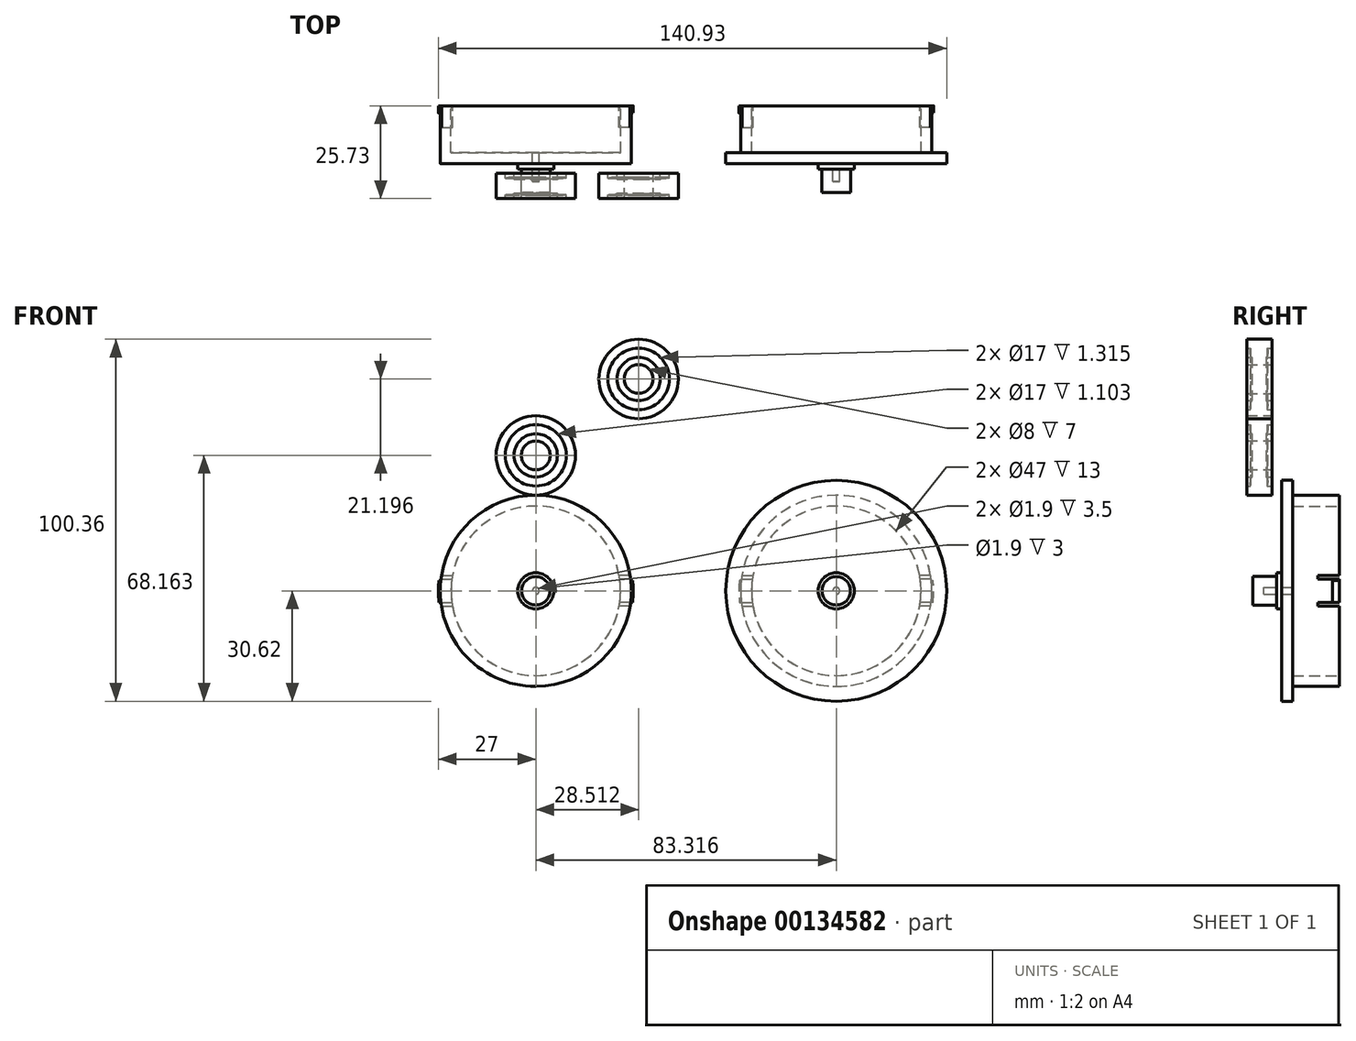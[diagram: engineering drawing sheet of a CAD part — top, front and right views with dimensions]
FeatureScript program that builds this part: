
annotation { "Feature Type Name" : "Feature", "Feature Type Description" : "" }
export const myFeature = defineFeature(function(context is Context, id is Id, definition is map)
    precondition{}
    {
        {
            var Q0;
            Q0=qCreatedBy(makeId("Front.planeOp"),FACE);
            var sketch = newSketch(context, id + "F0", { "sketchPlane" : qUnion([Q0])});
            skCircle(sketch, "E0", {"center": v(0, 0) * mm, "radius": 26.5 * mm});
            skSolve(sketch);
        }
        {
            var Q0;
            Q0 = qSketchRegion(id + "F0", true);
            extrude(context, id + "F1", {"entities" : qUnion([Q0]), "depth" : 16 * mm});
        }
        {
            var Q0;
            Q0=qCreatedBy(makeId("Front.planeOp"),FACE);
            var sketch = newSketch(context, id + "F2", { "sketchPlane" : qUnion([Q0])});
            skCircle(sketch, "E1", {"center": v(0, 0) * mm, "radius": 3.95 * mm});
            skSolve(sketch);
        }
        {
            var Q0;
            Q0 = qSketchRegion(id + "F2", true);
            extrude(context, id + "F3", {"entities" : qUnion([Q0]), "operationType" : NewBodyOperationType.ADD, "depth" : 24 * mm});
        }
        {
            var Q0;
            Q0=makeQuery(id+"F1.opExtrude","CAP_FACE",FACE,{"disambiguationData":[OSD([sQuery(id+"F0.wireOp",EDGE,"E0")])],"isStart":true});
            shell(context, id + "F4", {"entities" : qUnion([Q0]), "thickness" : 3 * mm});
        }
        {
            var Q0;
            Q0=qCreatedBy(makeId("Front.planeOp"),FACE);
            var sketch = newSketch(context, id + "F5", { "sketchPlane" : qUnion([Q0])});
            skArc(sketch, "E2", {"start": v(-26.85, 2.81) * mm, "mid": v(-27, -0.2) * mm, "end": v(-26.81, -3.19) * mm});
            skArc(sketch, "E3.MirrorCS", {"start": v(26.85, 2.81) * mm, "mid": v(27, -0.2) * mm, "end": v(26.81, -3.19) * mm});
            skLineSegment(sketch, "E4", {"start": v(-26.81, -3.19) * mm, "end": v(-26.2, -3.19) * mm});
            skLineSegment(sketch, "E5", {"start": v(-26.2, -3.19) * mm, "end": v(-26.2, 2.81) * mm});
            skLineSegment(sketch, "E6", {"start": v(-26.2, 2.81) * mm, "end": v(-26.85, 2.81) * mm});
            skLineSegment(sketch, "E7.MirrorCS", {"start": v(26.2, -3.19) * mm, "end": v(26.2, 2.81) * mm});
            skLineSegment(sketch, "E8.MirrorCS", {"start": v(26.81, -3.19) * mm, "end": v(26.2, -3.19) * mm});
            skLineSegment(sketch, "E9.MirrorCS", {"start": v(26.2, 2.81) * mm, "end": v(26.85, 2.81) * mm});
            skSolve(sketch);
        }
        {
            var Q0;
            Q0 = qSketchRegion(id + "F5", true);
            extrude(context, id + "F6", {"entities" : qUnion([Q0]), "operationType" : NewBodyOperationType.ADD, "depth" : 2 * mm});
        }
        {
            var Q0;
            Q0=makeQuery(id+"F6.boolean.opBoolean","MERGE",FACE,{"derivedFrom":[makeQuery(id+"F1.opExtrude","CAP_FACE",FACE,{"disambiguationData":[OSD([sQuery(id+"F0.wireOp",EDGE,"E0")])],"isStart":true}),makeQuery(id+"F6.opExtrude","CAP_FACE",FACE,{"disambiguationData":[OSD([sQuery(id+"F5.wireOp",EDGE,"E2"),sQuery(id+"F5.wireOp",EDGE,"E4"),sQuery(id+"F5.wireOp",EDGE,"E5"),sQuery(id+"F5.wireOp",EDGE,"E6")])],"isStart":true}),makeQuery(id+"F6.opExtrude","CAP_FACE",FACE,{"disambiguationData":[OSD([sQuery(id+"F5.wireOp",EDGE,"E3.MirrorCS"),sQuery(id+"F5.wireOp",EDGE,"E7.MirrorCS"),sQuery(id+"F5.wireOp",EDGE,"E8.MirrorCS"),sQuery(id+"F5.wireOp",EDGE,"E9.MirrorCS")])],"isStart":true})]});
            var sketch = newSketch(context, id + "F7", { "sketchPlane" : qUnion([Q0])});
            skLineSegment(sketch, "E10.bottom", {"start": v(26.3, -3.19) * mm, "end": v(23.11, -3.19) * mm});
            skLineSegment(sketch, "E10.top", {"start": v(26.3, -4.26) * mm, "end": v(23.11, -4.26) * mm});
            skLineSegment(sketch, "E10.left", {"start": v(26.3, -3.19) * mm, "end": v(26.3, -4.26) * mm});
            skLineSegment(sketch, "E10.right", {"start": v(23.11, -3.19) * mm, "end": v(23.11, -4.26) * mm});
            skLineSegment(sketch, "E11.MirrorCS", {"start": v(26.3, 3.19) * mm, "end": v(26.3, 4.26) * mm});
            skLineSegment(sketch, "E12.MirrorCS", {"start": v(26.3, 4.26) * mm, "end": v(23.11, 4.26) * mm});
            skLineSegment(sketch, "E13.MirrorCS", {"start": v(23.11, 3.19) * mm, "end": v(23.11, 4.26) * mm});
            skLineSegment(sketch, "E14.MirrorCS", {"start": v(26.3, 3.19) * mm, "end": v(23.11, 3.19) * mm});
            skLineSegment(sketch, "E15.MirrorCS", {"start": v(-23.11, -3.19) * mm, "end": v(-23.11, -4.26) * mm});
            skLineSegment(sketch, "E16.MirrorCS", {"start": v(-26.3, -4.26) * mm, "end": v(-23.11, -4.26) * mm});
            skLineSegment(sketch, "E17.MirrorCS", {"start": v(-26.3, -3.19) * mm, "end": v(-23.11, -3.19) * mm});
            skLineSegment(sketch, "E18.MirrorCS", {"start": v(-26.3, -3.19) * mm, "end": v(-26.3, -4.26) * mm});
            skLineSegment(sketch, "E19.MirrorCS", {"start": v(-23.11, 3.19) * mm, "end": v(-23.11, 4.26) * mm});
            skLineSegment(sketch, "E20.MirrorCS", {"start": v(-26.3, 3.19) * mm, "end": v(-23.11, 3.19) * mm});
            skLineSegment(sketch, "E21.MirrorCS", {"start": v(-26.3, 4.26) * mm, "end": v(-23.11, 4.26) * mm});
            skLineSegment(sketch, "E22.MirrorCS", {"start": v(-26.3, 3.19) * mm, "end": v(-26.3, 4.26) * mm});
            skSolve(sketch);
        }
        {
            var Q0;
            Q0 = qSketchRegion(id + "F7", true);
            extrude(context, id + "F8", {"entities" : qUnion([Q0]), "operationType" : NewBodyOperationType.REMOVE, "oppositeDirection" : true, "depth" : 6 * mm});
        }
        {
            var Q0;
            Q0=makeQuery(id+"F1.opExtrude","CAP_FACE",FACE,{"disambiguationData":[OSD([sQuery(id+"F0.wireOp",EDGE,"E0")])],"isStart":false});
            var sketch = newSketch(context, id + "F9", { "sketchPlane" : qUnion([Q0])});
            skCircle(sketch, "E23", {"center": v(0, 0) * mm, "radius": 5 * mm});
            skSolve(sketch);
        }
        {
            var Q0;
            Q0 = qSketchRegion(id + "F9", true);
            extrude(context, id + "F10", {"entities" : qUnion([Q0]), "operationType" : NewBodyOperationType.ADD, "depth" : 1.5 * mm});
        }
        {
            var Q0;
            Q0=makeQuery(id+"F1.opExtrude","SWEPT_BODY",BODY,{"disambiguationData":[OSD([sQuery(id+"F0.wireOp",EDGE,"E0")])]});
            transform(context, id + "F11", {"entities" : qUnion([Q0]), "transformType" : TransformType.TRANSLATION_3D, "dx" : 0 * mm, "dy" : 0 * mm, "dz" : 0 * mm, "makeCopy" : true});
        }
        {
            var Q0;
            Q0=makeQuery(id+"F11.opPattern","COPY",BODY,{"derivedFrom":makeQuery(id+"F1.opExtrude","SWEPT_BODY",BODY,{"disambiguationData":[OSD([sQuery(id+"F0.wireOp",EDGE,"E0")])]}),"instanceName":"1"});
            deleteBodies(context, id + "F12", {"entities" : qUnion([Q0])});
        }
        {
            var Q0;
            Q0=makeQuery(id+"F1.opExtrude","SWEPT_BODY",BODY,{"disambiguationData":[OSD([sQuery(id+"F0.wireOp",EDGE,"E0")])]});
            transform(context, id + "F13", {"entities" : qUnion([Q0]), "transformType" : TransformType.TRANSLATION_3D, "dx" : 83.32 * mm, "dy" : 0 * mm, "dz" : 0 * mm, "makeCopy" : true});
        }
        {
            var Q0;
            Q0=qCreatedBy(makeId("Front.planeOp"),FACE);
            var sketch = newSketch(context, id + "F14", { "sketchPlane" : qUnion([Q0])});
            skCircle(sketch, "E24", {"center": v(-54.65, 51.4) * mm, "radius": 11 * mm});
            skSolve(sketch);
        }
        {
            var Q0;
            Q0=makeQuery(id+"F14.imprint","IMPRINT",FACE,{"disambiguationData":[TD([[makeQuery(id+"F14.imprint","IMPRINT",EDGE,{"derivedFrom":sQuery(id+"F14.wireOp",EDGE,"E24")}),1.0]])]});
            extrude(context, id + "F15", {"entities" : qUnion([Q0]), "depth" : 7 * mm});
        }
        {
            var Q0;
            Q0=qCreatedBy(makeId("Front.planeOp"),FACE);
            var sketch = newSketch(context, id + "F16", { "sketchPlane" : qUnion([Q0])});
            skCircle(sketch, "E25", {"center": v(-54.65, 51.4) * mm, "radius": 4 * mm});
            skSolve(sketch);
        }
        {
            var Q0;
            Q0=makeQuery(id+"F16.imprint","IMPRINT",FACE,{"disambiguationData":[TD([[makeQuery(id+"F16.imprint","IMPRINT",EDGE,{"derivedFrom":sQuery(id+"F16.wireOp",EDGE,"E25")}),1.0]])]});
            extrude(context, id + "F17", {"entities" : qUnion([Q0]), "operationType" : NewBodyOperationType.REMOVE, "endBound" : BoundingType.THROUGH_ALL, "depth" : 25 * mm});
        }
        {
            var Q0;
            Q0=makeQuery(id+"F15.opExtrude","SWEPT_BODY",BODY,{"disambiguationData":[OSD([sQuery(id+"F14.wireOp",EDGE,"E24")])]});
            transform(context, id + "F18", {"entities" : qUnion([Q0]), "transformType" : TransformType.TRANSLATION_3D, "dx" : 34.78 * mm, "dy" : 0 * mm, "dz" : 0 * mm, "makeCopy" : true});
        }
        {
            var Q0;
            Q0=qCreatedBy(makeId("Right.planeOp"),FACE);
            var sketch = newSketch(context, id + "F19", { "sketchPlane" : qUnion([Q0])});
            skLineSegment(sketch, "E26.bottom", {"start": v(-18.73, 43.54) * mm, "end": v(-25.73, 43.54) * mm});
            skLineSegment(sketch, "E26.top", {"start": v(-18.73, 41.54) * mm, "end": v(-25.73, 41.54) * mm});
            skLineSegment(sketch, "E26.left", {"start": v(-18.73, 43.54) * mm, "end": v(-18.73, 41.54) * mm});
            skLineSegment(sketch, "E26.right", {"start": v(-25.73, 43.54) * mm, "end": v(-25.73, 41.54) * mm});
            skLineSegment(sketch, "E27.bottom", {"start": v(-18.73, 48.54) * mm, "end": v(-25.73, 48.54) * mm});
            skLineSegment(sketch, "E27.top", {"start": v(-18.73, 46.04) * mm, "end": v(-25.73, 46.04) * mm});
            skLineSegment(sketch, "E27.left", {"start": v(-18.73, 48.54) * mm, "end": v(-18.73, 46.04) * mm});
            skLineSegment(sketch, "E27.right", {"start": v(-25.73, 48.54) * mm, "end": v(-25.73, 46.04) * mm});
            skCircle(sketch, "E28", {"center": v(-22.34, 45.04) * mm, "radius": 2.5 * mm});
            skLineSegment(sketch, "E29", {"start": v(-8.97, 37.54) * mm, "end": v(-40.4, 37.54) * mm, "construction": true});
            skSolve(sketch);
        }
        {
            var Q0;
            Q0=makeQuery(id+"F19.imprint","IMPRINT",FACE,{"disambiguationData":[TD([[makeQuery(id+"F19.imprint","IMPRINT",EDGE,{"derivedFrom":sQuery(id+"F19.wireOp",EDGE,"E26.top")}),-1.0]])]});
            var Q1;
            Q1=makeQuery(id+"F19.imprint","IMPRINT",FACE,{"disambiguationData":[TD([[makeQuery(id+"F19.imprint","IMPRINT",EDGE,{"derivedFrom":sQuery(id+"F19.wireOp",EDGE,"E27.bottom")}),1.0]])]});
            var Q2;
            {var subQ0=sQuery(id+"F19.wireOp",EDGE,"E28");var subQ1=sQuery(id+"F19.wireOp",EDGE,"E27.top");var subQ2=makeQuery(id+"F19.imprint","INTERSECT",VERTEX,{"disambiguationData":[OD(0.0)],"derivedFrom":[subQ1,subQ0]});Q2=makeQuery(id+"F19.imprint","IMPRINT",FACE,{"disambiguationData":[TD([[makeQuery(id+"F19.imprint","IMPRINT",EDGE,{"disambiguationData":[TD([[subQ2,-1.0]])],"derivedFrom":subQ1}),-1.0]])]});}
            var Q3;
            {var subQ0=sQuery(id+"F19.wireOp",EDGE,"E28");var subQ1=sQuery(id+"F19.wireOp",EDGE,"E26.bottom");var subQ2=makeQuery(id+"F19.imprint","INTERSECT",VERTEX,{"disambiguationData":[OD(0.0)],"derivedFrom":[subQ1,subQ0]});Q3=makeQuery(id+"F19.imprint","IMPRINT",FACE,{"disambiguationData":[TD([[makeQuery(id+"F19.imprint","IMPRINT",EDGE,{"disambiguationData":[TD([[subQ2,-1.0]])],"derivedFrom":subQ1}),-1.0]])]});}
            var Q4;
            {var subQ0=sQuery(id+"F19.wireOp",EDGE,"E28");var subQ1=sQuery(id+"F19.wireOp",EDGE,"E26.bottom");var subQ2=makeQuery(id+"F19.imprint","INTERSECT",VERTEX,{"disambiguationData":[OD(0.0)],"derivedFrom":[subQ1,subQ0]});Q4=makeQuery(id+"F19.imprint","IMPRINT",FACE,{"disambiguationData":[TD([[makeQuery(id+"F19.imprint","IMPRINT",EDGE,{"disambiguationData":[TD([[subQ2,-1.0]])],"derivedFrom":subQ1}),1.0]])]});}
            var Q5;
            Q5=sQuery(id+"F19.wireOp",EDGE,"E29");
            revolve(context, id + "F20", {"entities" : qUnion([Q0, Q1, Q2, Q3, Q4]), "axis" : qUnion([Q5]), "revolveType" : RevolveType.FULL});
        }
        {
            var Q0;
            Q0=makeQuery(id+"F18.opPattern","COPY",BODY,{"derivedFrom":makeQuery(id+"F15.opExtrude","SWEPT_BODY",BODY,{"disambiguationData":[OSD([sQuery(id+"F14.wireOp",EDGE,"E24")])]}),"instanceName":"1"});
            var Q1;
            Q1=makeQuery(id+"F15.opExtrude","SWEPT_BODY",BODY,{"disambiguationData":[OSD([sQuery(id+"F14.wireOp",EDGE,"E24")])]});
            deleteBodies(context, id + "F21", {"entities" : qUnion([Q0, Q1])});
        }
        {
            var Q0;
            Q0=makeQuery(id+"F20.opRevolve","SWEPT_BODY",BODY,{"disambiguationData":[OSD([sQuery(id+"F19.wireOp",EDGE,"E26.bottom"),sQuery(id+"F19.wireOp",EDGE,"E26.top"),sQuery(id+"F19.wireOp",EDGE,"E26.left"),sQuery(id+"F19.wireOp",EDGE,"E26.right"),sQuery(id+"F19.wireOp",EDGE,"E27.bottom"),sQuery(id+"F19.wireOp",EDGE,"E27.top"),sQuery(id+"F19.wireOp",EDGE,"E27.left"),sQuery(id+"F19.wireOp",EDGE,"E27.right"),sQuery(id+"F19.wireOp",EDGE,"E28")])]});
            transform(context, id + "F22", {"entities" : qUnion([Q0]), "transformType" : TransformType.TRANSLATION_3D, "dx" : 28.51 * mm, "dy" : 0 * mm, "dz" : 21.2 * mm, "makeCopy" : true});
        }
        {
            var Q0;
            Q0=makeQuery(id+"F13.opPattern","COPY",FACE,{"derivedFrom":makeQuery(id+"F1.opExtrude","CAP_FACE",FACE,{"disambiguationData":[OSD([sQuery(id+"F0.wireOp",EDGE,"E0")])],"isStart":false}),"instanceName":"1"});
            var sketch = newSketch(context, id + "F23", { "sketchPlane" : qUnion([Q0])});
            skCircle(sketch, "E30", {"center": v(83.32, 0) * mm, "radius": 30.62 * mm});
            skSolve(sketch);
        }
        {
            var Q0;
            Q0 = qSketchRegion(id + "F23", true);
            extrude(context, id + "F24", {"entities" : qUnion([Q0]), "operationType" : NewBodyOperationType.ADD, "oppositeDirection" : true, "depth" : 3 * mm});
        }
    });
